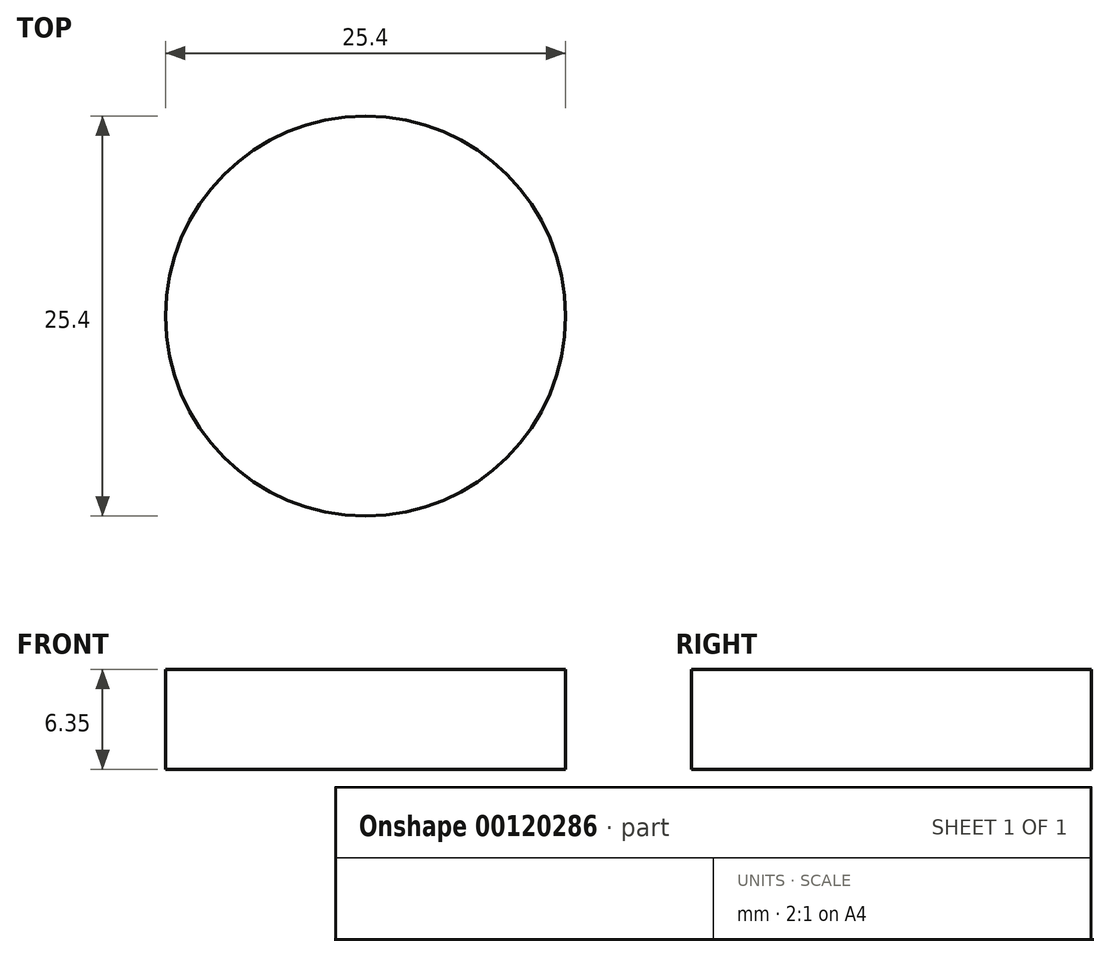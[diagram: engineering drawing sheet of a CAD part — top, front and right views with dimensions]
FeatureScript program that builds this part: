
annotation { "Feature Type Name" : "Feature", "Feature Type Description" : "" }
export const myFeature = defineFeature(function(context is Context, id is Id, definition is map)
    precondition{}
    {
        {
            var Q0;
            Q0=qCreatedBy(makeId("Top.planeOp"),FACE);
            var sketch = newSketch(context, id + "F0", { "sketchPlane" : qUnion([Q0])});
            skCircle(sketch, "E0", {"center": v(0, 0) * mm, "radius": 12.7 * mm});
            skSolve(sketch);
        }
        {
            var Q0;
            Q0 = qSketchRegion(id + "F0", true);
            extrude(context, id + "F1", {"entities" : qUnion([Q0]), "depth" : 6.35 * mm});
        }
    });
